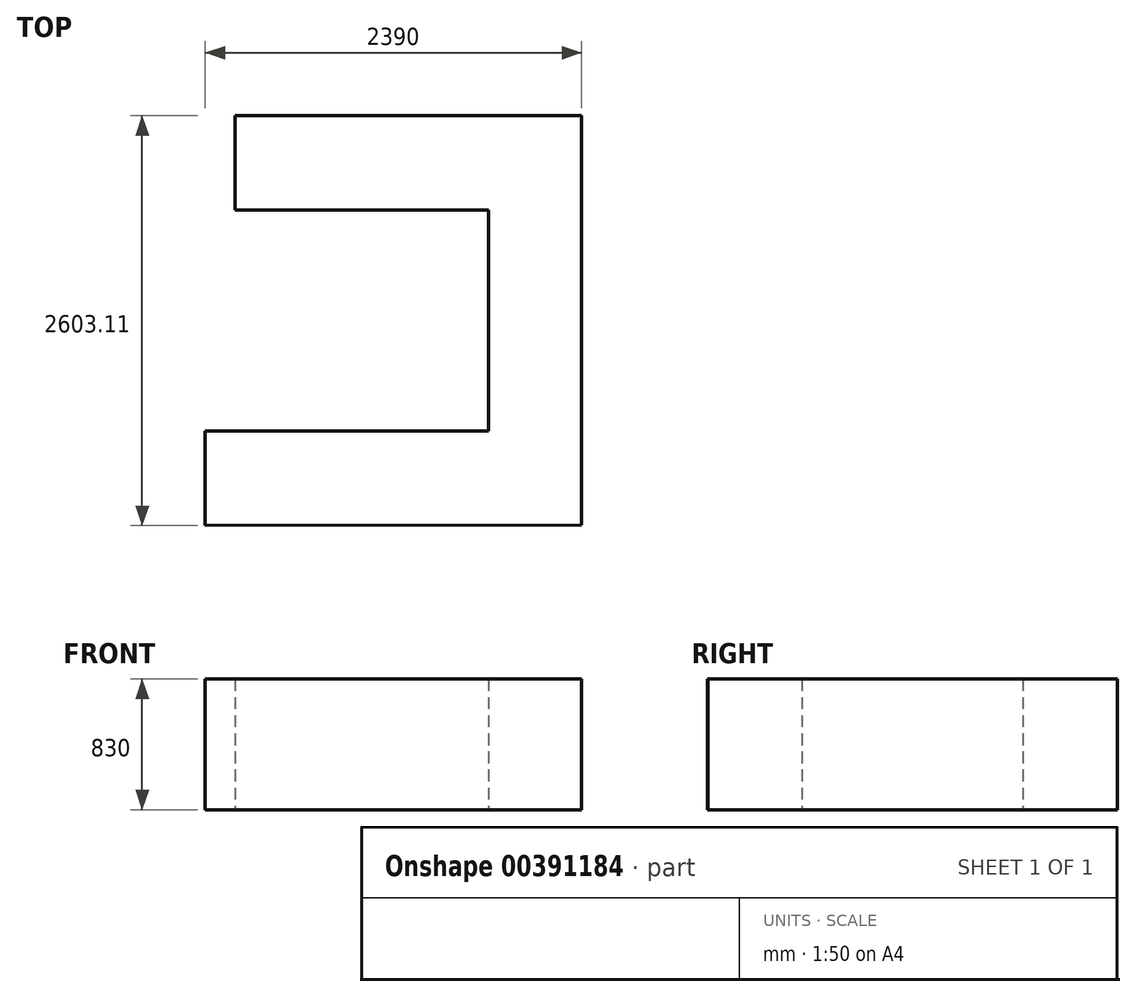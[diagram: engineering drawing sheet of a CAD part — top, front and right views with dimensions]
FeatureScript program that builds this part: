
annotation { "Feature Type Name" : "Feature", "Feature Type Description" : "" }
export const myFeature = defineFeature(function(context is Context, id is Id, definition is map)
    precondition{}
    {
        {
            var Q0;
            Q0=qCreatedBy(makeId("Top.planeOp"),FACE);
            var sketch = newSketch(context, id + "F0", { "sketchPlane" : qUnion([Q0])});
            skLineSegment(sketch, "E0", {"start": v(977.44, -1082.68) * mm, "end": v(977.44, 1517.32) * mm});
            skLineSegment(sketch, "E1", {"start": v(977.44, 1517.32) * mm, "end": v(-1222.56, 1517.32) * mm});
            skLineSegment(sketch, "E2", {"start": v(-1222.56, 1517.32) * mm, "end": v(-1222.56, 917.32) * mm});
            skLineSegment(sketch, "E3", {"start": v(-1222.56, 917.32) * mm, "end": v(387.44, 917.32) * mm});
            skLineSegment(sketch, "E4", {"start": v(387.44, 917.32) * mm, "end": v(387.44, -485.8) * mm});
            skLineSegment(sketch, "E5", {"start": v(387.44, -485.8) * mm, "end": v(-1412.56, -485.8) * mm});
            skLineSegment(sketch, "E6", {"start": v(-1412.56, -485.8) * mm, "end": v(-1412.56, -1085.8) * mm});
            skLineSegment(sketch, "E7", {"start": v(-1412.56, -1085.8) * mm, "end": v(977.44, -1082.68) * mm});
            skSolve(sketch);
        }
        {
            var Q0;
            Q0=makeQuery(id+"F0.imprint","IMPRINT",FACE,{"disambiguationData":[TD([[makeQuery(id+"F0.imprint","IMPRINT",EDGE,{"derivedFrom":sQuery(id+"F0.wireOp",EDGE,"E0")}),1.0]])]});
            extrude(context, id + "F1", {"entities" : qUnion([Q0]), "depth" : 830 * mm});
        }
    });
